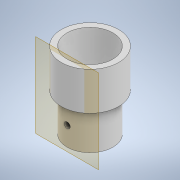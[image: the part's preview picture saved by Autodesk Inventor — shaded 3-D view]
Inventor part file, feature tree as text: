
AUTODESK INVENTOR PART (.ipt)
format: ipt  version: 2022.3 (Build 263350000, 350)  size: 130,560 bytes
history: native  units: mm
features: sketch x2, extrude x2, plane x1, hole x1, mirror x1
ambient origin geometry x8: Origin, YZ Plane, XZ Plane, XY Plane, X Axis, Y Axis, Z Axis, Center Point
bodies: Solid1 (feature_tree)
feature tree (7):
  sketch  "Sketch1"  dims[d0=24.0mm d1=30.0mm]
  extrude  "Extrusion1"  Depth=30.0mm
  extrude  "Extrusion2"  Depth=1.2mm TaperAngle=0.0deg
  plane  "Work Plane1"
  hole  "Hole1"  [1 undecoded]
  mirror  "Mirror1"
  sketch  "Sketch2"  dims[d2=20.0mm d3=0.0mm d4=20.0mm d5=0.0mm d6=12.0mm d7=5.0mm d8=2.2mm d9=6.0mm d10=3.1mm d11=4.6mm d12=90.0deg d13=1.2mm d14=0.0mm]
note: 1 required parameter value undecoded (feature->parameter linkage not recoverable at this tier; creation-order binding heuristic only, values carry confidence <= 0.55)
